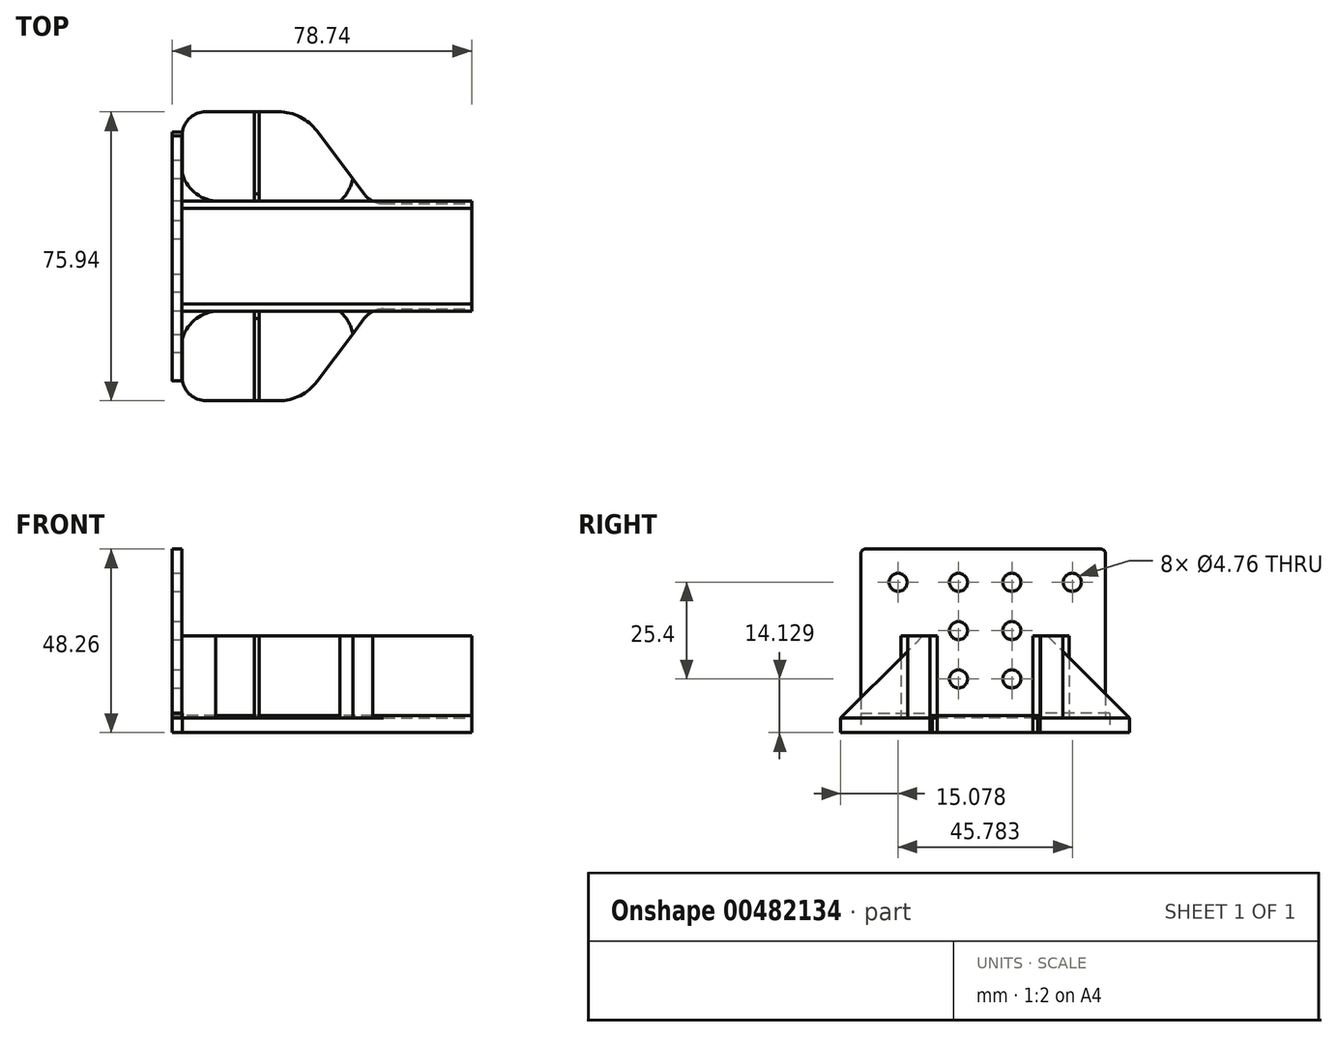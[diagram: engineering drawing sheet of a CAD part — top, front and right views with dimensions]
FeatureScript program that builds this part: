
annotation { "Feature Type Name" : "Feature", "Feature Type Description" : "" }
export const myFeature = defineFeature(function(context is Context, id is Id, definition is map)
    precondition{}
    {
        {
            var Q0;
            Q0=qCreatedBy(makeId("Top.planeOp"),FACE);
            var sketch = newSketch(context, id + "F0", { "sketchPlane" : qUnion([Q0])});
            skLineSegment(sketch, "E0", {"start": v(-38.1, 0) * mm, "end": v(38.1, 0) * mm, "construction": true});
            skLineSegment(sketch, "E1", {"start": v(-38.1, 12.57) * mm, "end": v(38.1, 12.57) * mm});
            skLineSegment(sketch, "E2.bottom", {"start": v(-31.75, 37.97) * mm, "end": v(-12.7, 37.97) * mm});
            skLineSegment(sketch, "E2.top", {"start": v(-38.1, 12.57) * mm, "end": v(12.7, 12.57) * mm});
            skLineSegment(sketch, "E2.left", {"start": v(-38.1, 31.62) * mm, "end": v(-38.1, 12.57) * mm});
            skPoint(sketch, "E3.visualSharp", {"position": v(-38.1, 37.97) * mm});
            skArc(sketch, "E3.filletArc", {"start": v(-31.75, 37.97) * mm, "mid": v(-36.24, 36.11) * mm, "end": v(-38.1, 31.62) * mm});
            skLineSegment(sketch, "E4", {"start": v(9.84, 16.38) * mm, "end": v(-2.54, 32.9) * mm});
            skPoint(sketch, "E5.visualSharp", {"position": v(-6.35, 37.97) * mm});
            skArc(sketch, "E5.filletArc", {"start": v(-2.54, 32.9) * mm, "mid": v(-7.02, 36.63) * mm, "end": v(-12.7, 37.97) * mm});
            skLineSegment(sketch, "E6.0", {"start": v(14.92, 13.84) * mm, "end": v(38.1, 13.84) * mm});
            skLineSegment(sketch, "E7", {"start": v(38.1, 13.84) * mm, "end": v(38.1, 12.57) * mm});
            skPoint(sketch, "E8.orphan", {"position": v(-38.1, 13.84) * mm});
            skPoint(sketch, "E9.visualSharp", {"position": v(11.75, 13.84) * mm});
            skArc(sketch, "E9.filletArc", {"start": v(9.84, 16.38) * mm, "mid": v(12.08, 14.51) * mm, "end": v(14.92, 13.84) * mm});
            skLineSegment(sketch, "E10.MirrorCS", {"start": v(38.1, -13.84) * mm, "end": v(38.1, -12.57) * mm});
            skArc(sketch, "E11.MirrorCS", {"start": v(9.84, -16.38) * mm, "mid": v(12.08, -14.51) * mm, "end": v(14.92, -13.84) * mm});
            skPoint(sketch, "E12.MirrorP", {"position": v(11.75, -13.84) * mm});
            skPoint(sketch, "E13.MirrorP", {"position": v(-38.1, -13.84) * mm});
            skLineSegment(sketch, "E14.MirrorCS", {"start": v(-38.1, -31.62) * mm, "end": v(-38.1, -12.57) * mm});
            skArc(sketch, "E15.MirrorCS", {"start": v(-31.75, -37.97) * mm, "mid": v(-36.24, -36.11) * mm, "end": v(-38.1, -31.62) * mm});
            skPoint(sketch, "E16.MirrorP", {"position": v(-6.35, -37.97) * mm});
            skLineSegment(sketch, "E17.MirrorCS", {"start": v(9.84, -16.38) * mm, "end": v(-2.54, -32.9) * mm});
            skLineSegment(sketch, "E18.MirrorCS", {"start": v(14.92, -13.84) * mm, "end": v(38.1, -13.84) * mm});
            skLineSegment(sketch, "E19.MirrorCS", {"start": v(-38.1, -12.57) * mm, "end": v(12.7, -12.57) * mm});
            skLineSegment(sketch, "E20.MirrorCS", {"start": v(-31.75, -37.97) * mm, "end": v(-12.7, -37.97) * mm});
            skLineSegment(sketch, "E21.MirrorCS", {"start": v(-38.1, -12.57) * mm, "end": v(38.1, -12.57) * mm});
            skArc(sketch, "E22.MirrorCS", {"start": v(-2.54, -32.9) * mm, "mid": v(-7.02, -36.63) * mm, "end": v(-12.7, -37.97) * mm});
            skPoint(sketch, "E23.MirrorP", {"position": v(-38.1, -37.97) * mm});
            skSolve(sketch);
        }
        {
            var Q0;
            Q0 = qSketchRegion(id + "F0", true);
            extrude(context, id + "F1", {"entities" : qUnion([Q0]), "depth" : 3.8 * mm});
        }
        {
            var Q0;
            Q0=makeQuery(id+"F1.opExtrude","CAP_FACE",FACE,{"disambiguationData":[OSD([sQuery(id+"F0.wireOp",EDGE,"E1"),sQuery(id+"F0.wireOp",EDGE,"E2.bottom"),sQuery(id+"F0.wireOp",EDGE,"E2.top"),sQuery(id+"F0.wireOp",EDGE,"E2.left"),sQuery(id+"F0.wireOp",EDGE,"E3.filletArc"),sQuery(id+"F0.wireOp",EDGE,"E4"),sQuery(id+"F0.wireOp",EDGE,"E5.filletArc"),sQuery(id+"F0.wireOp",EDGE,"E6.0"),sQuery(id+"F0.wireOp",EDGE,"E7"),sQuery(id+"F0.wireOp",EDGE,"E9.filletArc")])],"isStart":false});
            var sketch = newSketch(context, id + "F2", { "sketchPlane" : qUnion([Q0])});
            skLineSegment(sketch, "E24.bottom", {"start": v(-40.64, 31.62) * mm, "end": v(-38.1, 31.62) * mm});
            skLineSegment(sketch, "E24.top", {"start": v(-40.64, -32.7) * mm, "end": v(-38.1, -32.7) * mm});
            skLineSegment(sketch, "E24.left", {"start": v(-40.64, 31.62) * mm, "end": v(-40.64, -32.7) * mm});
            skLineSegment(sketch, "E24.right", {"start": v(-38.1, 31.62) * mm, "end": v(-38.1, -32.7) * mm});
            skSolve(sketch);
        }
        {
            var Q0;
            Q0 = qSketchRegion(id + "F2", true);
            extrude(context, id + "F3", {"entities" : qUnion([Q0]), "depth" : 44.45 * mm});
        }
        {
            var Q0;
            Q0=makeQuery(id+"F3.opExtrude","CAP_EDGE",EDGE,{"disambiguationData":[OSD([sQuery(id+"F2.wireOp",EDGE,"E24.bottom")])],"isStart":false});
            fillet(context, id + "F4", {"entities" : qUnion([Q0]), "radius" : 1.27 * mm, "tangentPropagation" : true, "allowEdgeOverflow" : false});
        }
        {
            var Q0;
            Q0=makeQuery(id+"F3.opExtrude","CAP_EDGE",EDGE,{"disambiguationData":[OSD([sQuery(id+"F2.wireOp",EDGE,"E24.top")])],"isStart":false});
            fillet(context, id + "F5", {"entities" : qUnion([Q0]), "radius" : 1.27 * mm, "tangentPropagation" : true, "allowEdgeOverflow" : false});
        }
        {
            var Q0;
            Q0=qCreatedBy(makeId("Top.planeOp"),FACE);
            var sketch = newSketch(context, id + "F6", { "sketchPlane" : qUnion([Q0])});
            skLineSegment(sketch, "E25", {"start": v(-38.1, 0) * mm, "end": v(38.1, 0) * mm, "construction": true});
            skLineSegment(sketch, "E26.bottom", {"start": v(38.1, 14.48) * mm, "end": v(-38.09, 14.48) * mm});
            skLineSegment(sketch, "E26.top", {"start": v(38.1, 12.57) * mm, "end": v(-38.09, 12.57) * mm});
            skLineSegment(sketch, "E26.left", {"start": v(38.1, 14.48) * mm, "end": v(38.1, 12.57) * mm});
            skLineSegment(sketch, "E26.right", {"start": v(-38.09, 14.48) * mm, "end": v(-38.09, 12.57) * mm});
            skLineSegment(sketch, "E27.MirrorCS", {"start": v(38.1, -14.48) * mm, "end": v(38.1, -12.57) * mm});
            skLineSegment(sketch, "E28.MirrorCS", {"start": v(-38.09, -14.48) * mm, "end": v(-38.09, -12.57) * mm});
            skLineSegment(sketch, "E29.MirrorCS", {"start": v(38.1, -12.57) * mm, "end": v(-38.09, -12.57) * mm});
            skLineSegment(sketch, "E30.MirrorCS", {"start": v(38.1, -14.48) * mm, "end": v(-38.09, -14.48) * mm});
            skSolve(sketch);
        }
        {
            var Q0;
            Q0 = qSketchRegion(id + "F6", true);
            extrude(context, id + "F7", {"entities" : qUnion([Q0]), "depth" : 25.4 * mm});
        }
        {
            var Q0;
            Q0=makeQuery(id+"F1.opExtrude","CAP_FACE",FACE,{"disambiguationData":[OSD([sQuery(id+"F0.wireOp",EDGE,"E1"),sQuery(id+"F0.wireOp",EDGE,"E2.bottom"),sQuery(id+"F0.wireOp",EDGE,"E2.top"),sQuery(id+"F0.wireOp",EDGE,"E2.left"),sQuery(id+"F0.wireOp",EDGE,"E3.filletArc"),sQuery(id+"F0.wireOp",EDGE,"E4"),sQuery(id+"F0.wireOp",EDGE,"E5.filletArc"),sQuery(id+"F0.wireOp",EDGE,"E6.0"),sQuery(id+"F0.wireOp",EDGE,"E7"),sQuery(id+"F0.wireOp",EDGE,"E9.filletArc")])],"isStart":false});
            var sketch = newSketch(context, id + "F8", { "sketchPlane" : qUnion([Q0])});
            skArc(sketch, "E31", {"start": v(-38.1, 22.1) * mm, "mid": v(-34.86, 16.88) * mm, "end": v(-29.21, 14.48) * mm});
            skLineSegment(sketch, "E32", {"start": v(-38.1, 0) * mm, "end": v(38.1, 0) * mm, "construction": true});
            skArc(sketch, "E33.MirrorCS", {"start": v(-38.1, -22.1) * mm, "mid": v(-34.86, -16.88) * mm, "end": v(-29.21, -14.48) * mm});
            skLineSegment(sketch, "E34", {"start": v(-38.1, 22.1) * mm, "end": v(-38.1, 14.47) * mm});
            skLineSegment(sketch, "E35", {"start": v(-38.1, 14.47) * mm, "end": v(-29.21, 14.48) * mm});
            skLineSegment(sketch, "E36.MirrorCS", {"start": v(-38.1, -14.47) * mm, "end": v(-29.21, -14.48) * mm});
            skLineSegment(sketch, "E37.MirrorCS", {"start": v(-38.1, -22.1) * mm, "end": v(-38.1, -14.47) * mm});
            skSolve(sketch);
        }
        {
            var Q0;
            Q0 = qSketchRegion(id + "F8", true);
            extrude(context, id + "F9", {"entities" : qUnion([Q0]), "depth" : 21.59 * mm});
        }
        {
            var Q0;
            Q0=makeQuery(id+"F1.opExtrude","CAP_FACE",FACE,{"disambiguationData":[OSD([sQuery(id+"F0.wireOp",EDGE,"E1"),sQuery(id+"F0.wireOp",EDGE,"E2.bottom"),sQuery(id+"F0.wireOp",EDGE,"E2.top"),sQuery(id+"F0.wireOp",EDGE,"E2.left"),sQuery(id+"F0.wireOp",EDGE,"E3.filletArc"),sQuery(id+"F0.wireOp",EDGE,"E4"),sQuery(id+"F0.wireOp",EDGE,"E5.filletArc"),sQuery(id+"F0.wireOp",EDGE,"E6.0"),sQuery(id+"F0.wireOp",EDGE,"E7"),sQuery(id+"F0.wireOp",EDGE,"E9.filletArc")])],"isStart":false});
            var sketch = newSketch(context, id + "F10", { "sketchPlane" : qUnion([Q0])});
            skArc(sketch, "E38", {"start": v(3.4, 14.48) * mm, "mid": v(5.64, 17.13) * mm, "end": v(6.84, 20.4) * mm});
            skPoint(sketch, "E39.endSnap0", {"position": v(12.08, 14.51) * mm});
            skLineSegment(sketch, "E40", {"start": v(12.08, 14.51) * mm, "end": v(3.4, 14.48) * mm});
            skLineSegment(sketch, "E41", {"start": v(-38.1, 0) * mm, "end": v(38.1, 0) * mm, "construction": true});
            skArc(sketch, "E42.MirrorCS", {"start": v(3.4, -14.48) * mm, "mid": v(5.64, -17.13) * mm, "end": v(6.84, -20.4) * mm});
            skLineSegment(sketch, "E43.MirrorCS", {"start": v(12.08, -14.51) * mm, "end": v(3.4, -14.48) * mm});
            skLineSegment(sketch, "E44", {"start": v(6.84, 20.4) * mm, "end": v(9.84, 16.38) * mm});
            skArc(sketch, "E45", {"start": v(9.84, 16.38) * mm, "mid": v(10.85, 15.32) * mm, "end": v(12.08, 14.51) * mm});
            skLineSegment(sketch, "E46.MirrorCS", {"start": v(6.84, -20.4) * mm, "end": v(9.84, -16.38) * mm});
            skArc(sketch, "E47.MirrorCS", {"start": v(9.84, -16.38) * mm, "mid": v(10.85, -15.32) * mm, "end": v(12.08, -14.51) * mm});
            skSolve(sketch);
        }
        {
            var Q0;
            Q0 = qSketchRegion(id + "F10", true);
            extrude(context, id + "F11", {"entities" : qUnion([Q0]), "depth" : 21.59 * mm});
        }
        {
            var Q0;
            Q0=makeQuery(id+"F1.opExtrude","CAP_FACE",FACE,{"disambiguationData":[OSD([sQuery(id+"F0.wireOp",EDGE,"E1"),sQuery(id+"F0.wireOp",EDGE,"E2.bottom"),sQuery(id+"F0.wireOp",EDGE,"E2.top"),sQuery(id+"F0.wireOp",EDGE,"E2.left"),sQuery(id+"F0.wireOp",EDGE,"E3.filletArc"),sQuery(id+"F0.wireOp",EDGE,"E4"),sQuery(id+"F0.wireOp",EDGE,"E5.filletArc"),sQuery(id+"F0.wireOp",EDGE,"E6.0"),sQuery(id+"F0.wireOp",EDGE,"E7"),sQuery(id+"F0.wireOp",EDGE,"E9.filletArc")])],"isStart":false});
            var sketch = newSketch(context, id + "F12", { "sketchPlane" : qUnion([Q0])});
            skLineSegment(sketch, "E48.bottom", {"start": v(-19.05, 37.97) * mm, "end": v(-17.78, 37.97) * mm});
            skLineSegment(sketch, "E48.top", {"start": v(-19.05, 14.48) * mm, "end": v(-17.78, 14.48) * mm});
            skLineSegment(sketch, "E48.left", {"start": v(-19.05, 37.97) * mm, "end": v(-19.05, 14.48) * mm});
            skLineSegment(sketch, "E48.right", {"start": v(-17.78, 37.97) * mm, "end": v(-17.78, 14.48) * mm});
            skLineSegment(sketch, "E49", {"start": v(-38.1, 0) * mm, "end": v(38.1, 0) * mm, "construction": true});
            skLineSegment(sketch, "E50.MirrorCS", {"start": v(-19.05, -37.97) * mm, "end": v(-17.78, -37.97) * mm});
            skLineSegment(sketch, "E51.MirrorCS", {"start": v(-19.05, -14.48) * mm, "end": v(-17.78, -14.48) * mm});
            skLineSegment(sketch, "E52.MirrorCS", {"start": v(-19.05, -37.97) * mm, "end": v(-19.05, -14.48) * mm});
            skLineSegment(sketch, "E53.MirrorCS", {"start": v(-17.78, -37.97) * mm, "end": v(-17.78, -14.48) * mm});
            skSolve(sketch);
        }
        {
            var Q0;
            Q0 = qSketchRegion(id + "F12", true);
            extrude(context, id + "F13", {"entities" : qUnion([Q0]), "depth" : 21.59 * mm});
        }
        {
            var Q0;
            Q0=makeQuery(id+"F13.opExtrude","CAP_EDGE",EDGE,{"disambiguationData":[OSD([sQuery(id+"F12.wireOp",EDGE,"E48.bottom")])],"isStart":false});
            var Q1;
            Q1=makeQuery(id+"F13.opExtrude","CAP_EDGE",EDGE,{"disambiguationData":[OSD([sQuery(id+"F12.wireOp",EDGE,"E50.MirrorCS")])],"isStart":false});
            chamfer(context, id + "F14", {"entities" : qUnion([Q0, Q1]), "width" : 21.59 * mm, "tangentPropagation" : true});
        }
        {
            var Q0;
            Q0=makeQuery(id+"F3.opExtrude","SWEPT_FACE",FACE,{"disambiguationData":[OSD([sQuery(id+"F2.wireOp",EDGE,"E24.right")])]});
            var sketch = newSketch(context, id + "F15", { "sketchPlane" : qUnion([Q0])});
            skCircle(sketch, "E54", {"center": v(22.9, 39.53) * mm, "radius": 2.38 * mm});
            skLineSegment(sketch, "E55", {"start": v(0, 54.31) * mm, "end": v(0, -24.2) * mm, "construction": true});
            skCircle(sketch, "E56", {"center": v(7.02, 39.53) * mm, "radius": 2.38 * mm});
            skCircle(sketch, "E57", {"center": v(7.02, 26.83) * mm, "radius": 2.38 * mm});
            skCircle(sketch, "E58", {"center": v(7.02, 14.13) * mm, "radius": 2.38 * mm});
            skCircle(sketch, "E59.MirrorC", {"center": v(-22.9, 39.53) * mm, "radius": 2.38 * mm});
            skCircle(sketch, "E60.MirrorC", {"center": v(-7.02, 26.83) * mm, "radius": 2.38 * mm});
            skCircle(sketch, "E61.MirrorC", {"center": v(-7.02, 14.13) * mm, "radius": 2.38 * mm});
            skCircle(sketch, "E62.MirrorC", {"center": v(-7.02, 39.53) * mm, "radius": 2.38 * mm});
            skSolve(sketch);
        }
        {
            var Q0;
            Q0 = qSketchRegion(id + "F15", true);
            extrude(context, id + "F16", {"entities" : qUnion([Q0]), "operationType" : NewBodyOperationType.REMOVE, "endBound" : BoundingType.THROUGH_ALL, "oppositeDirection" : true, "depth" : 25.4 * mm});
        }
        {
            var Q0;
            Q0=makeQuery(id+"F1.opExtrude","CAP_FACE",FACE,{"disambiguationData":[OSD([sQuery(id+"F0.wireOp",EDGE,"E10.MirrorCS"),sQuery(id+"F0.wireOp",EDGE,"E11.MirrorCS"),sQuery(id+"F0.wireOp",EDGE,"E14.MirrorCS"),sQuery(id+"F0.wireOp",EDGE,"E15.MirrorCS"),sQuery(id+"F0.wireOp",EDGE,"E17.MirrorCS"),sQuery(id+"F0.wireOp",EDGE,"E18.MirrorCS"),sQuery(id+"F0.wireOp",EDGE,"E20.MirrorCS"),sQuery(id+"F0.wireOp",EDGE,"E21.MirrorCS"),sQuery(id+"F0.wireOp",EDGE,"E22.MirrorCS")])],"isStart":true});
            var sketch = newSketch(context, id + "F17", { "sketchPlane" : qUnion([Q0])});
            skLineSegment(sketch, "E63.bottom", {"start": v(38.1, 14.48) * mm, "end": v(-40.64, 14.48) * mm});
            skLineSegment(sketch, "E63.top", {"start": v(38.1, -14.48) * mm, "end": v(-40.64, -14.48) * mm});
            skLineSegment(sketch, "E63.left", {"start": v(38.1, 14.48) * mm, "end": v(38.1, -14.48) * mm});
            skLineSegment(sketch, "E63.right", {"start": v(-40.64, 14.48) * mm, "end": v(-40.64, -14.48) * mm});
            skSolve(sketch);
        }
        {
            var Q0;
            Q0 = qSketchRegion(id + "F17", true);
            extrude(context, id + "F18", {"entities" : qUnion([Q0]), "oppositeDirection" : true, "depth" : 4.44 * mm});
        }
        {
            var Q0;
            Q0=makeQuery(id+"F18.opExtrude","CAP_FACE",FACE,{"disambiguationData":[OSD([sQuery(id+"F17.wireOp",EDGE,"E63.bottom"),sQuery(id+"F17.wireOp",EDGE,"E63.top"),sQuery(id+"F17.wireOp",EDGE,"E63.left"),sQuery(id+"F17.wireOp",EDGE,"E63.right")])],"isStart":true});
            var sketch = newSketch(context, id + "F19", { "sketchPlane" : qUnion([Q0])});
            skLineSegment(sketch, "E64", {"start": v(-38.1, 0) * mm, "end": v(38.1, 0) * mm, "construction": true});
            skLineSegment(sketch, "E65.bottom", {"start": v(-40.64, 32.7) * mm, "end": v(-38, 32.7) * mm});
            skLineSegment(sketch, "E65.top", {"start": v(-40.64, 14.48) * mm, "end": v(-38, 14.48) * mm});
            skLineSegment(sketch, "E65.left", {"start": v(-40.64, 32.7) * mm, "end": v(-40.64, 14.48) * mm});
            skLineSegment(sketch, "E65.right", {"start": v(-38, 32.7) * mm, "end": v(-38, 14.48) * mm});
            skLineSegment(sketch, "E66.MirrorCS", {"start": v(-40.64, -32.7) * mm, "end": v(-40.64, -14.48) * mm});
            skLineSegment(sketch, "E67.MirrorCS", {"start": v(-38, -32.7) * mm, "end": v(-38, -14.48) * mm});
            skLineSegment(sketch, "E68.MirrorCS", {"start": v(-40.64, -32.7) * mm, "end": v(-38, -32.7) * mm});
            skLineSegment(sketch, "E69.MirrorCS", {"start": v(-40.64, -14.48) * mm, "end": v(-38, -14.48) * mm});
            skSolve(sketch);
        }
        {
            var Q0;
            Q0 = qSketchRegion(id + "F19", true);
            extrude(context, id + "F20", {"entities" : qUnion([Q0]), "oppositeDirection" : true, "depth" : 5.08 * mm});
        }
    });
